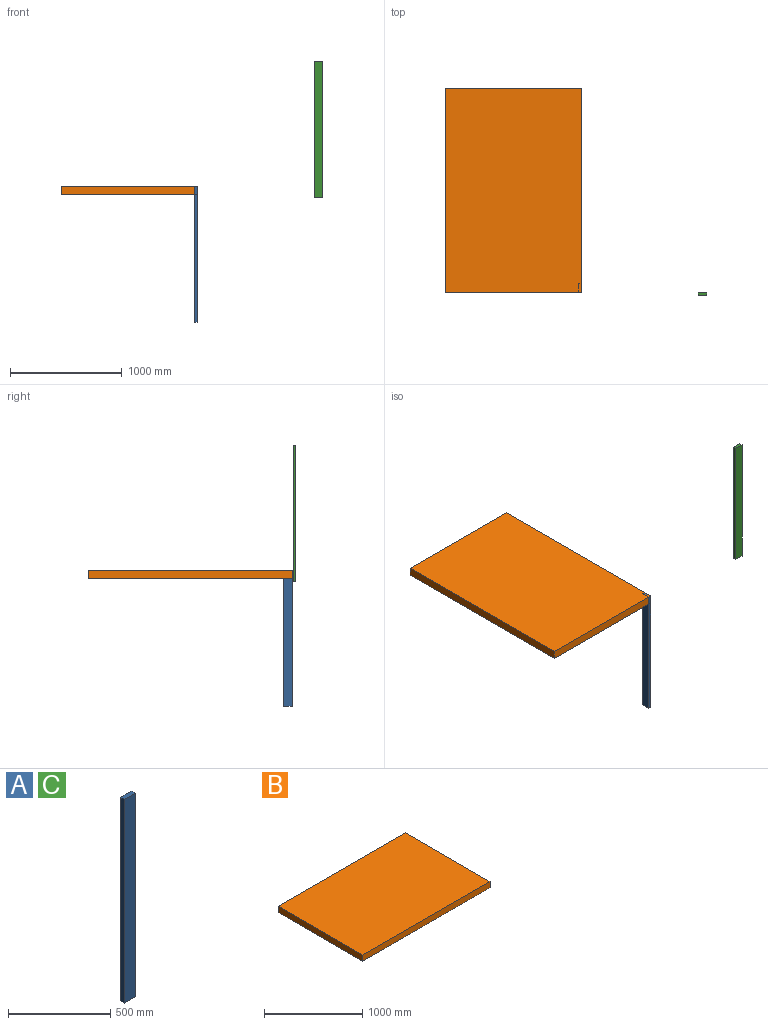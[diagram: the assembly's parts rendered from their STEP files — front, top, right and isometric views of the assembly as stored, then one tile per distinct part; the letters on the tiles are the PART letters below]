
ASSEMBLY  parts=3 mates=2
PART A: 6 faces, bbox 76.2x25.4x1219.2 mm
  f0: plane 76.2x25.4mm, normal (0,0,-1), area 1935.5mm2, adj f1,f3,f4,f5
  f1: plane 1219.2x25.4mm, normal (1,0,0), area 30967.7mm2, adj f0,f2,f4,f5
  f2: plane 76.2x25.4mm, normal (0,0,1), area 1935.5mm2, adj f1,f3,f4,f5
  f3: plane 1219.2x25.4mm, normal (-1,0,0), area 30967.7mm2, adj f0,f2,f4,f5
  f4: plane 1219.2x76.2mm, normal (0,-1,0), area 92903mm2, adj f0,f1,f2,f3
  f5: plane 1219.2x76.2mm, normal (0,1,0), area 92903mm2, adj f0,f1,f2,f3
PART B: 6 faces, bbox 1828.8x1219.2x76.2 mm
  f0: plane 1828.8x76.2mm, normal (0,-1,0), area 139354.6mm2, adj f1,f3,f4,f5
  f1: plane 1219.2x76.2mm, normal (1,0,0), area 92903mm2, adj f0,f2,f4,f5
  f2: plane 1828.8x76.2mm, normal (0,1,0), area 139354.6mm2, adj f1,f3,f4,f5
  f3: plane 1219.2x76.2mm, normal (-1,0,0), area 92903mm2, adj f0,f2,f4,f5
  f4: plane 1828.8x1219.2mm, normal (0,0,1), area 2229673mm2, adj f0,f1,f2,f3
  f5: plane 1828.8x1219.2mm, normal (0,0,-1), area 2229673mm2, adj f0,f1,f2,f3
PART C: same geometry as A
PLACE A rot(axis=(0,0,1),90deg) t=(-118.95,-623.21,247.89)mm
PLACE B rot(axis=(0.71,-0.71,0),180deg) t=(-703.15,253.09,857.49)mm
PLACE C rot(axis=(1,0,0),0deg) t=(993.55,-669.74,1360.01)mm
MATE fastened B.f4 <-> B.f0  axis (0,0,-1) through (-93.55,-661.31,781.29)mm
MATE fastened B.f1 <-> A.f3  axis (0,1,0) through (-93.55,-661.31,857.49)mm
